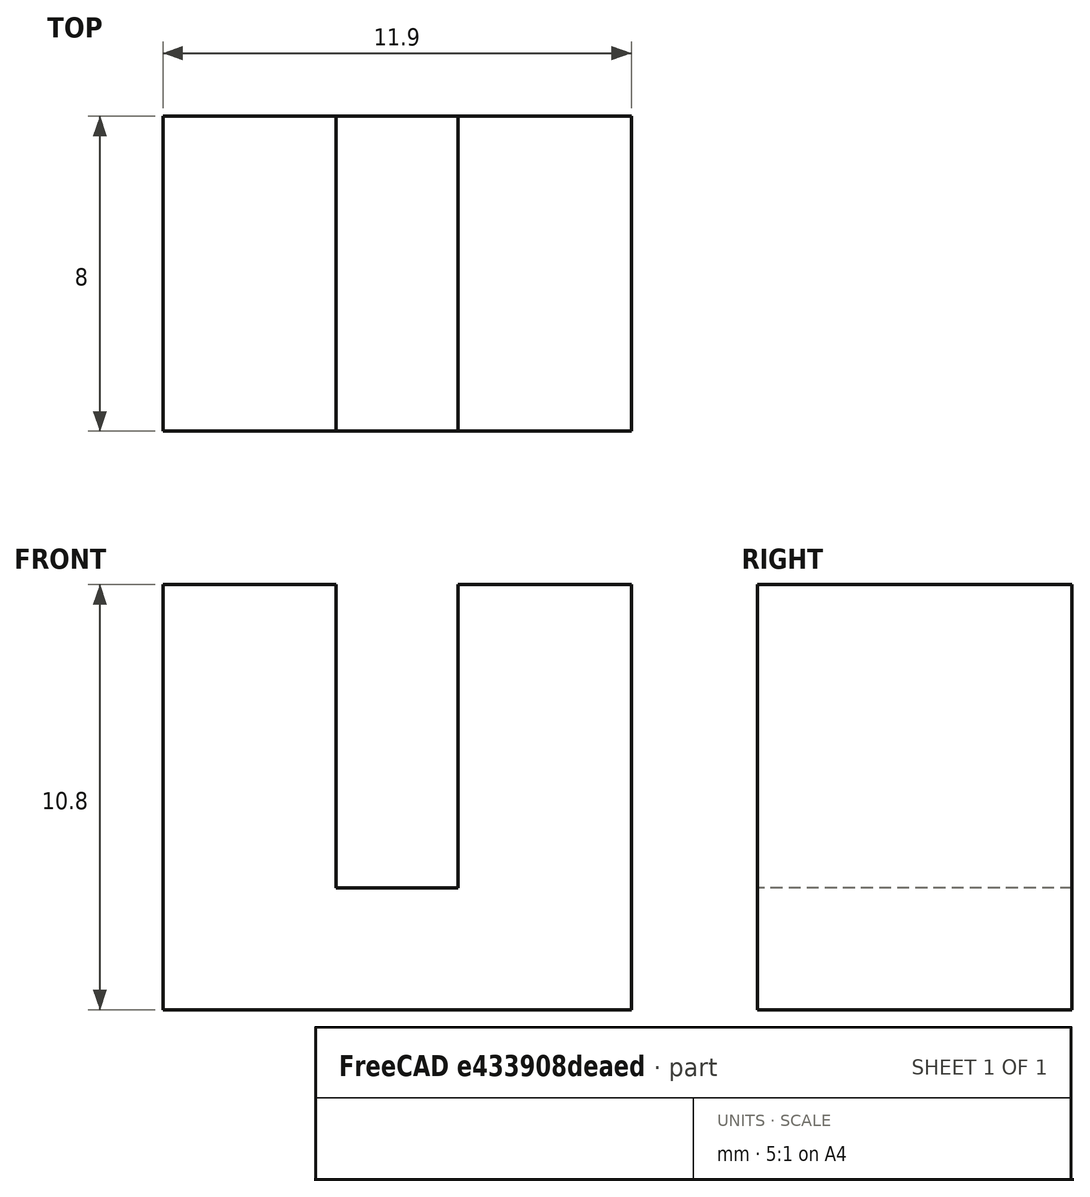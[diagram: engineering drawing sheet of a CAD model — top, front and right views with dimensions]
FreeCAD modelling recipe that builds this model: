
FCSTD DOCUMENT  (FreeCAD 0.18.4R)
Label: tcst1103_socket
License: All rights reserved
LicenseURL: http://en.wikipedia.org/wiki/All_rights_reserved
objects: Sketcher::SketchObject×1, PartDesign::Pad×1, PartDesign::Body×1
note: 4 computed .brp shape members not serialized (recipe doc carries the construction recipe); baked Part::Feature solids carry a one-line shape summary decoded from their .brp

FEATURE [Sketcher::SketchObject] Sketch
  MapMode = 5
  Placement = pos=(0,0,0) rot=(1,0,0;1.5708rad)
  Support = -> [XZ_Plane]
  sketch-geometry (8):
    g0: LineSegment StartX=0 StartY=0 StartZ=0 EndX=0 EndY=10.8 EndZ=0
    g1: LineSegment StartX=0 StartY=10.8 StartZ=0 EndX=4.4 EndY=10.8 EndZ=0
    g2: LineSegment StartX=4.4 StartY=10.8 StartZ=0 EndX=4.4 EndY=3.1 EndZ=0
    g3: LineSegment StartX=4.4 StartY=3.1 StartZ=0 EndX=7.5 EndY=3.1 EndZ=0
    g4: LineSegment StartX=7.5 StartY=3.1 StartZ=0 EndX=7.5 EndY=10.8 EndZ=0
    g5: LineSegment StartX=7.5 StartY=10.8 StartZ=0 EndX=11.9 EndY=10.8 EndZ=0
    g6: LineSegment StartX=11.9 StartY=10.8 StartZ=0 EndX=11.9 EndY=0 EndZ=0
    g7: LineSegment StartX=0 StartY=0 StartZ=0 EndX=11.9 EndY=0 EndZ=0
  constraints (23):
    c: DistanceY(g0,g0) = 10.8
    c: Coincident(g-1,g0)
    c: Coincident(g7,g0)
    c: Coincident(g1,g0)
    c: Vertical(g0)
    c: Horizontal(g1)
    c: Coincident(g1,g2)
    c: DistanceY(g2,g2) = 7.7
    c: Coincident(g2,g3)
    c: Horizontal(g3)
    c: DistanceX(g3,g3) = 3.1
    c: Coincident(g4,g3)
    c: Vertical(g4)
    c: DistanceY(g4,g4) = 7.7
    c: Coincident(g5,g4)
    c: Horizontal(g5)
    c: Coincident(g6,g5)
    c: Vertical(g6)
    c: DistanceX(g5,g5) = 4.4
    c: DistanceX(g1,g1) = 4.4
    c: Vertical(g2)
    c: Coincident(g6,g7)
    c: Horizontal(g7)
FEATURE [PartDesign::Pad] Pad
  Length = 8
  Length2 = 100
  Placement = pos=(0,0,0) rot=(1,0,0;1.5708rad)
  Profile = -> Sketch
  Type = 0
FEATURE [PartDesign::Body] Body
  Group = -> [Sketch,Pad]
  Origin = -> Origin
  Tip = -> Pad
